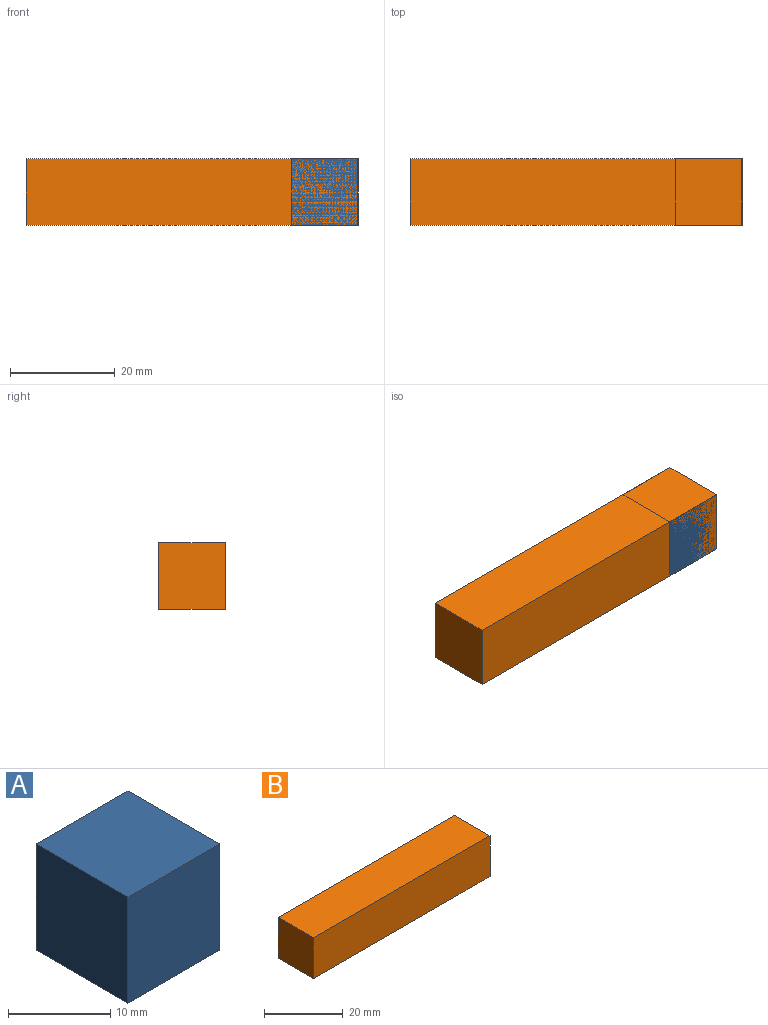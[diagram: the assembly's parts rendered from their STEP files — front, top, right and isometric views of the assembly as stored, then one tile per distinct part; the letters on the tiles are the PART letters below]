
ASSEMBLY  parts=2 mates=1
PART A: 6 faces, bbox 12.7x12.7x12.7 mm
  f0: plane 12.7x12.7mm, normal (0,0,-1), area 161.3mm2, adj f1,f3,f4,f5
  f1: plane 12.7x12.7mm, normal (1,0,0), area 161.3mm2, adj f0,f2,f4,f5
  f2: plane 12.7x12.7mm, normal (0,0,1), area 161.3mm2, adj f1,f3,f4,f5
  f3: plane 12.7x12.7mm, normal (-1,0,0), area 161.3mm2, adj f0,f2,f4,f5
  f4: plane 12.7x12.7mm, normal (0,-1,0), area 161.3mm2, adj f0,f1,f2,f3
  f5: plane 12.7x12.7mm, normal (0,1,0), area 161.3mm2, adj f0,f1,f2,f3
PART B: 6 faces, bbox 63.5x12.7x12.7 mm
  f0: plane 63.5x12.7mm, normal (0,0,-1), area 806.5mm2, adj f1,f3,f4,f5
  f1: plane 12.7x12.7mm, normal (1,0,0), area 161.3mm2, adj f0,f2,f4,f5
  f2: plane 63.5x12.7mm, normal (0,0,1), area 806.5mm2, adj f1,f3,f4,f5
  f3: plane 12.7x12.7mm, normal (-1,0,0), area 161.3mm2, adj f0,f2,f4,f5
  f4: plane 63.5x12.7mm, normal (0,-1,0), area 806.5mm2, adj f0,f1,f2,f3
  f5: plane 63.5x12.7mm, normal (0,1,0), area 806.5mm2, adj f0,f1,f2,f3
PLACE A t=(23.09,5.18,-103.38)mm
PLACE B t=(0.99,5.18,-31.2)mm
MATE fastened A.f1 <-> B.f1  axis (1,0,0) through (29.44,-1.17,-74.81)mm
